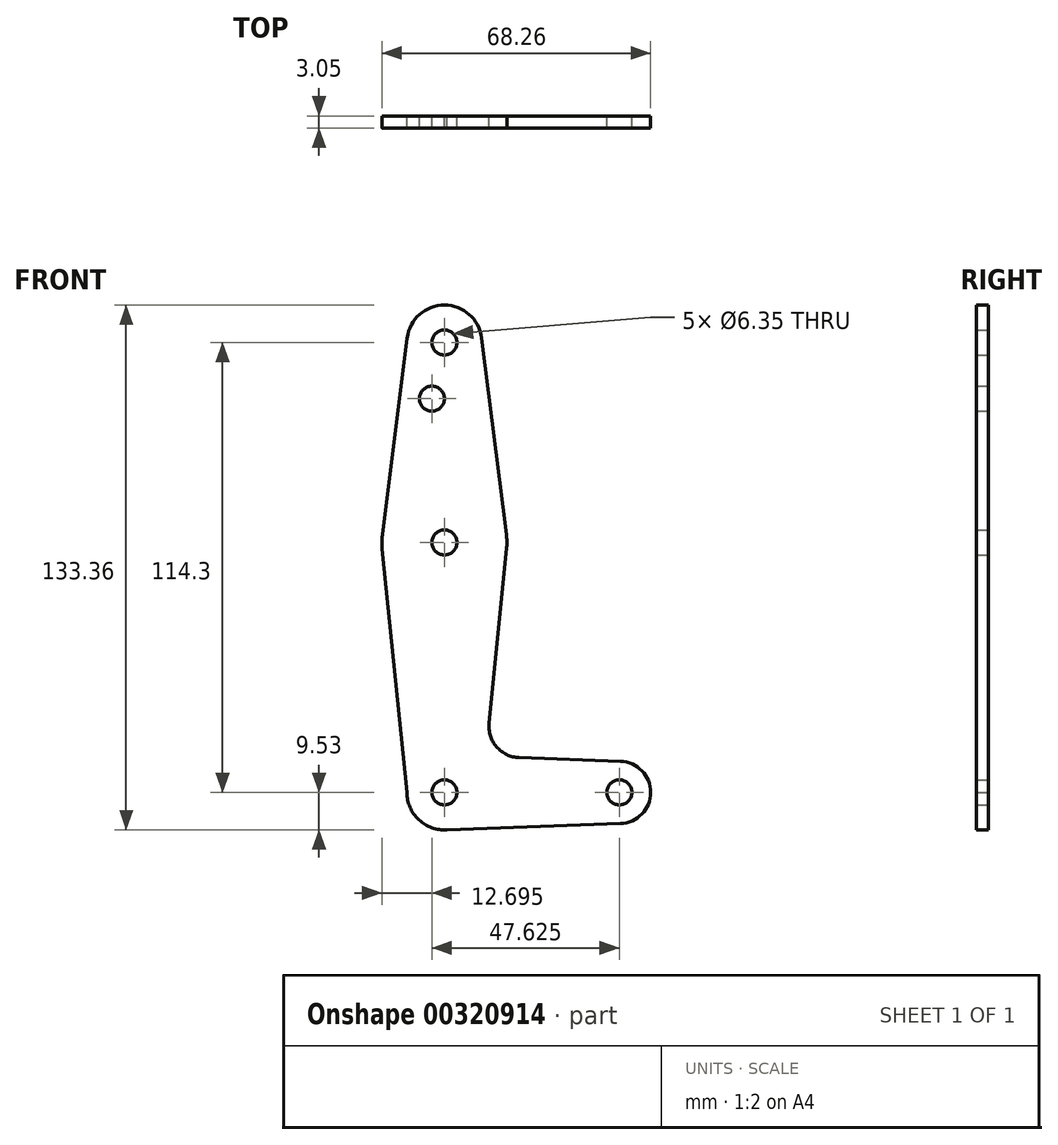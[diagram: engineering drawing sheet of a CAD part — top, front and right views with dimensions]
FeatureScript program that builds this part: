
annotation { "Feature Type Name" : "Feature", "Feature Type Description" : "" }
export const myFeature = defineFeature(function(context is Context, id is Id, definition is map)
    precondition{}
    {
        {
            var Q0;
            Q0=qCreatedBy(makeId("Front.planeOp"),FACE);
            var sketch = newSketch(context, id + "F0", { "sketchPlane" : qUnion([Q0])});
            skLineSegment(sketch, "E0", {"start": v(0, 114.3) * mm, "end": v(0, 0) * mm, "construction": true});
            skLineSegment(sketch, "E1", {"start": v(0, 0) * mm, "end": v(44.45, 0) * mm, "construction": true});
            skCircle(sketch, "E2", {"center": v(0, 0) * mm, "radius": 9.53 * mm});
            skCircle(sketch, "E3", {"center": v(0, 63.5) * mm, "radius": 15.88 * mm});
            skCircle(sketch, "E4", {"center": v(0, 114.3) * mm, "radius": 9.53 * mm});
            skCircle(sketch, "E5", {"center": v(44.45, 0) * mm, "radius": 7.94 * mm});
            skLineSegment(sketch, "E6", {"start": v(-9.52, 0) * mm, "end": v(-15.8, 61.9) * mm});
            skLineSegment(sketch, "E7", {"start": v(15.8, 61.91) * mm, "end": v(11.34, 17.59) * mm});
            skLineSegment(sketch, "E8", {"start": v(18.97, 8.85) * mm, "end": v(44.73, 7.93) * mm});
            skLineSegment(sketch, "E9", {"start": v(0, -9.53) * mm, "end": v(44.73, -7.93) * mm});
            skLineSegment(sketch, "E10", {"start": v(-9.45, 115.5) * mm, "end": v(-15.75, 65.48) * mm});
            skLineSegment(sketch, "E11", {"start": v(9.45, 115.5) * mm, "end": v(15.75, 65.48) * mm});
            skCircle(sketch, "E12", {"center": v(0, 114.3) * mm, "radius": 3.18 * mm});
            skCircle(sketch, "E13", {"center": v(0, 63.5) * mm, "radius": 3.18 * mm});
            skCircle(sketch, "E14", {"center": v(0, 0) * mm, "radius": 3.18 * mm});
            skCircle(sketch, "E15", {"center": v(44.45, 0) * mm, "radius": 3.18 * mm});
            skCircle(sketch, "E16", {"center": v(-3.17, 100.03) * mm, "radius": 3.18 * mm});
            skArc(sketch, "E17.filletArc", {"start": v(11.34, 17.59) * mm, "mid": v(13.26, 11.57) * mm, "end": v(18.97, 8.85) * mm});
            skSolve(sketch);
        }
        {
            var Q0;
            Q0 = qSketchRegion(id + "F0", true);
            extrude(context, id + "F1", {"entities" : qUnion([Q0]), "depth" : 3.05 * mm});
        }
    });
